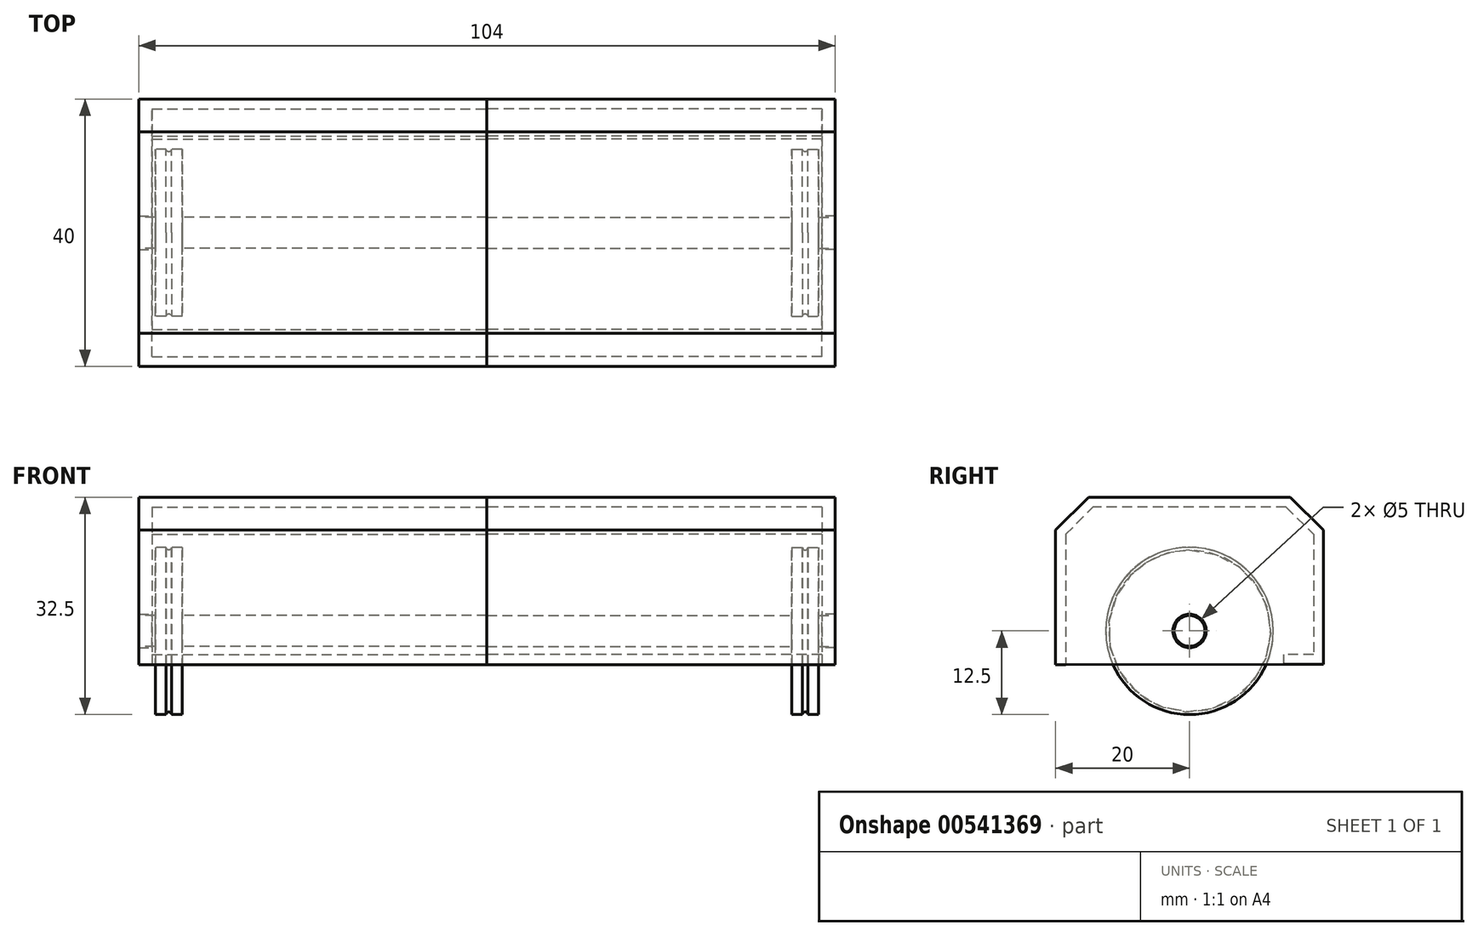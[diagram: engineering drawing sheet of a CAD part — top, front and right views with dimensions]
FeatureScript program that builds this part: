
annotation { "Feature Type Name" : "Feature", "Feature Type Description" : "" }
export const myFeature = defineFeature(function(context is Context, id is Id, definition is map)
    precondition{}
    {
        {
            var Q0;
            Q0=qCreatedBy(makeId("Right.planeOp"),FACE);
            var sketch = newSketch(context, id + "F0", { "sketchPlane" : qUnion([Q0])});
            skLineSegment(sketch, "E0", {"start": v(0, 0) * mm, "end": v(0, 20) * mm, "construction": true});
            skLineSegment(sketch, "E1", {"start": v(0, 20) * mm, "end": v(-15.05, 20) * mm});
            skCircle(sketch, "E2", {"center": v(0, 0) * mm, "radius": 12.5 * mm, "construction": true});
            skLineSegment(sketch, "E3", {"start": v(-20, 15.05) * mm, "end": v(-20, -5.07) * mm});
            skLineSegment(sketch, "E4", {"start": v(0, 20) * mm, "end": v(15.05, 20) * mm});
            skLineSegment(sketch, "E5", {"start": v(20, 15.05) * mm, "end": v(20, -5) * mm});
            skLineSegment(sketch, "E6", {"start": v(20, -5) * mm, "end": v(20, -5) * mm});
            skLineSegment(sketch, "E7", {"start": v(20, -5) * mm, "end": v(14, -5) * mm});
            skLineSegment(sketch, "E8.0", {"start": v(18.5, -3.5) * mm, "end": v(14, -3.5) * mm});
            skLineSegment(sketch, "E8.1", {"start": v(-18.5, 14.43) * mm, "end": v(-18.5, -5.07) * mm});
            skLineSegment(sketch, "E8.2", {"start": v(0.07, 18.5) * mm, "end": v(-14.43, 18.5) * mm});
            skLineSegment(sketch, "E8.3", {"start": v(0.07, 18.5) * mm, "end": v(14.43, 18.5) * mm});
            skLineSegment(sketch, "E8.4", {"start": v(18.5, 14.43) * mm, "end": v(18.5, -3.5) * mm});
            skLineSegment(sketch, "E9", {"start": v(-20, -5.07) * mm, "end": v(-18.5, -5.07) * mm});
            skLineSegment(sketch, "E10", {"start": v(14, -3.5) * mm, "end": v(14, -5) * mm});
            skPoint(sketch, "E11", {"position": v(-14.43, 18.5) * mm});
            skPoint(sketch, "E12", {"position": v(-18.5, 14.43) * mm});
            skLineSegment(sketch, "E13", {"start": v(-18.5, 14.43) * mm, "end": v(-14.43, 18.5) * mm});
            skPoint(sketch, "E14", {"position": v(-15.05, 20) * mm});
            skPoint(sketch, "E15", {"position": v(-20, 15.05) * mm});
            skLineSegment(sketch, "E16", {"start": v(-20, 15.05) * mm, "end": v(-15.05, 20) * mm});
            skLineSegment(sketch, "E17", {"start": v(-17.53, 17.53) * mm, "end": v(-16.46, 16.46) * mm, "construction": true});
            skPoint(sketch, "E18", {"position": v(14.43, 18.5) * mm});
            skPoint(sketch, "E19", {"position": v(18.5, 14.43) * mm});
            skPoint(sketch, "E20", {"position": v(15.05, 20) * mm});
            skPoint(sketch, "E21", {"position": v(20, 15.05) * mm});
            skLineSegment(sketch, "E22", {"start": v(14.43, 18.5) * mm, "end": v(18.5, 14.43) * mm});
            skLineSegment(sketch, "E23", {"start": v(15.05, 20) * mm, "end": v(20, 15.05) * mm});
            skPoint(sketch, "E24", {"position": v(16.46, 16.46) * mm});
            skPoint(sketch, "E25", {"position": v(17.53, 17.53) * mm});
            skLineSegment(sketch, "E26", {"start": v(16.46, 16.46) * mm, "end": v(17.53, 17.53) * mm, "construction": true});
            skSolve(sketch);
        }
        {
            var Q0;
            Q0=makeQuery(id+"F0.imprint","IMPRINT",FACE,{"disambiguationData":[TD([[makeQuery(id+"F0.imprint","IMPRINT",EDGE,{"derivedFrom":sQuery(id+"F0.wireOp",EDGE,"E1")}),1.0]])]});
            extrude(context, id + "F1", {"entities" : qUnion([Q0]), "depth" : 50 * mm, "offsetDistance" : 25 * mm});
        }
        {
            var Q0;
            Q0=makeQuery(id+"F1.opExtrude","CAP_FACE",FACE,{"disambiguationData":[OSD([sQuery(id+"F0.wireOp",EDGE,"E1"),sQuery(id+"F0.wireOp",EDGE,"E3"),sQuery(id+"F0.wireOp",EDGE,"E4"),sQuery(id+"F0.wireOp",EDGE,"E5"),sQuery(id+"F0.wireOp",EDGE,"E7"),sQuery(id+"F0.wireOp",EDGE,"E8.0"),sQuery(id+"F0.wireOp",EDGE,"E8.1"),sQuery(id+"F0.wireOp",EDGE,"E8.2"),sQuery(id+"F0.wireOp",EDGE,"E8.3"),sQuery(id+"F0.wireOp",EDGE,"E8.4"),sQuery(id+"F0.wireOp",EDGE,"E9"),sQuery(id+"F0.wireOp",EDGE,"E10")])],"isStart":false});
            var sketch = newSketch(context, id + "F2", { "sketchPlane" : qUnion([Q0])});
            skLineSegment(sketch, "E27.0.8", {"start": v(-20, -5.07) * mm, "end": v(-18.5, -5.07) * mm});
            skPoint(sketch, "E27.0.0.start.orphan", {"position": v(-14.43, 18.5) * mm});
            skPoint(sketch, "E27.0.1.start.orphan", {"position": v(14.43, 18.5) * mm});
            skPoint(sketch, "E27.0.2.start.orphan", {"position": v(18.5, -3.5) * mm});
            skPoint(sketch, "E27.0.3.start.orphan", {"position": v(14, -3.5) * mm});
            skCircle(sketch, "E28", {"center": v(0, 0) * mm, "radius": 2.5 * mm});
            skLineSegment(sketch, "E29.0", {"start": v(-20, 15.05) * mm, "end": v(-20, -5.07) * mm});
            skPoint(sketch, "E30.0", {"position": v(-17.53, 17.53) * mm});
            skLineSegment(sketch, "E31.0", {"start": v(-20, 15.05) * mm, "end": v(-15.05, 20) * mm});
            skLineSegment(sketch, "E32.0", {"start": v(0, 20) * mm, "end": v(-15.05, 20) * mm});
            skLineSegment(sketch, "E33.0", {"start": v(0, 20) * mm, "end": v(15.05, 20) * mm});
            skLineSegment(sketch, "E34.0", {"start": v(15.05, 20) * mm, "end": v(20, 15.05) * mm});
            skPoint(sketch, "E35.0", {"position": v(17.53, 17.53) * mm});
            skLineSegment(sketch, "E36.0", {"start": v(20, 15.05) * mm, "end": v(20, -5) * mm});
            skLineSegment(sketch, "E37.0", {"start": v(20, -5) * mm, "end": v(14, -5) * mm});
            skLineSegment(sketch, "E38", {"start": v(-18.5, -5.07) * mm, "end": v(14, -5) * mm});
            skSolve(sketch);
        }
        {
            var Q0;
            Q0 = qSketchRegion(id + "F2", true);
            extrude(context, id + "F3", {"entities" : qUnion([Q0]), "operationType" : NewBodyOperationType.ADD, "depth" : 2 * mm, "offsetDistance" : 25 * mm});
        }
        {
            var Q0;
            Q0=makeQuery(id+"F3.opExtrude","CAP_FACE",FACE,{"disambiguationData":[OSD([sQuery(id+"F2.wireOp",EDGE,"E27.0.5"),sQuery(id+"F2.wireOp",EDGE,"E27.0.6"),sQuery(id+"F2.wireOp",EDGE,"E27.0.7"),sQuery(id+"F2.wireOp",EDGE,"7a487413-c71e-4137-a8b7-0069e7eb67ab"),sQuery(id+"F2.wireOp",EDGE,"E28")])],"isStart":false});
            var sketch = newSketch(context, id + "F4", { "sketchPlane" : qUnion([Q0])});
            skCircle(sketch, "E39.0", {"center": v(0, 0) * mm, "radius": 2.3 * mm});
            skSolve(sketch);
        }
        {
            var Q0;
            Q0 = qSketchRegion(id + "F4", true);
            extrude(context, id + "F5", {"entities" : qUnion([Q0]), "oppositeDirection" : true, "depth" : 52 * mm, "offsetDistance" : 25 * mm});
        }
        {
            var Q0;
            Q0=makeQuery(id+"F3.opExtrude","CAP_FACE",FACE,{"disambiguationData":[OSD([sQuery(id+"F2.wireOp",EDGE,"E27.0.5"),sQuery(id+"F2.wireOp",EDGE,"E27.0.6"),sQuery(id+"F2.wireOp",EDGE,"E27.0.7"),sQuery(id+"F2.wireOp",EDGE,"7a487413-c71e-4137-a8b7-0069e7eb67ab"),sQuery(id+"F2.wireOp",EDGE,"E28")])],"isStart":false});
            cPlane(context, id + "F6", {"entities" : qUnion([Q0]), "cplaneType" : CPlaneType.OFFSET, "offset" : 2.5 * mm, "oppositeDirection" : true, "width" : 150 * mm, "height" : 150 * mm});
        }
        {
            var Q0;
            Q0=qCreatedBy(id+"F6.planeOp",FACE);
            var sketch = newSketch(context, id + "F7", { "sketchPlane" : qUnion([Q0])});
            skCircle(sketch, "E40.0", {"center": v(0, 0) * mm, "radius": 12.5 * mm});
            skSolve(sketch);
        }
        {
            var Q0;
            Q0 = qSketchRegion(id + "F7", true);
            extrude(context, id + "F8", {"entities" : qUnion([Q0]), "operationType" : NewBodyOperationType.ADD, "oppositeDirection" : true, "depth" : 4 * mm, "offsetDistance" : 25 * mm});
        }
        {
            var Q0;
            Q0=qCreatedBy(makeId("Top.planeOp"),FACE);
            cPlane(context, id + "F9", {"entities" : qUnion([Q0]), "cplaneType" : CPlaneType.OFFSET, "offset" : 0 * mm, "width" : 150 * mm, "height" : 150 * mm});
        }
        {
            var Q0;
            Q0=qCreatedBy(id+"F9.planeOp",FACE);
            var sketch = newSketch(context, id + "F10", { "sketchPlane" : qUnion([Q0])});
            skLineSegment(sketch, "E41", {"start": v(47.1, 12.5) * mm, "end": v(47.9, 12.5) * mm});
            skPoint(sketch, "E42.0.end.orphan", {"position": v(45.5, -12.5) * mm});
            skPoint(sketch, "E43.0.end.orphan", {"position": v(49.5, -12.5) * mm});
            skArc(sketch, "E44", {"start": v(47.1, 12.5) * mm, "mid": v(47.5, 12.1) * mm, "end": v(47.9, 12.5) * mm});
            skPoint(sketch, "E45.orphan", {"position": v(45.5, 12.5) * mm});
            skPoint(sketch, "E46.orphan", {"position": v(49.5, 12.5) * mm});
            skSolve(sketch);
        }
        {
            var Q0;
            Q0=makeQuery(id+"F8.opExtrude","CAP_FACE",FACE,{"disambiguationData":[OSD([sQuery(id+"F7.wireOp",EDGE,"E40.0")])],"isStart":true});
            cPlane(context, id + "F11", {"entities" : qUnion([Q0]), "cplaneType" : CPlaneType.OFFSET, "offset" : 2 * mm, "oppositeDirection" : true, "width" : 150 * mm, "height" : 150 * mm});
        }
        {
            var Q0;
            Q0=qCreatedBy(makeId("Top.planeOp"),FACE);
            var sketch = newSketch(context, id + "F12", { "sketchPlane" : qUnion([Q0])});
            skLineSegment(sketch, "E47", {"start": v(0, 0) * mm, "end": v(42.92, 0) * mm});
            skSolve(sketch);
        }
        {
            var Q0;
            Q0=makeQuery(id+"F10.imprint","IMPRINT",FACE,{"disambiguationData":[TD([[makeQuery(id+"F10.imprint","IMPRINT",EDGE,{"derivedFrom":sQuery(id+"F10.wireOp",EDGE,"E41")}),-1.0]])]});
            var Q1;
            Q1=sQuery(id+"F10.wireOp",EDGE,"E44");
            var Q2;
            Q2=sQuery(id+"F10.wireOp",EDGE,"E41");
            var Q3;
            Q3=sQuery(id+"F12.wireOp",EDGE,"E47");
            revolve(context, id + "F13", {"operationType" : NewBodyOperationType.REMOVE, "entities" : qUnion([Q0]), "surfaceEntities" : qUnion([Q1, Q2]), "axis" : qUnion([Q3]), "revolveType" : RevolveType.FULL});
        }
        {
            var Q0;
            Q0=makeQuery(id+"F1.opExtrude","SWEPT_BODY",BODY,{"disambiguationData":[OSD([sQuery(id+"F0.wireOp",EDGE,"E1"),sQuery(id+"F0.wireOp",EDGE,"E3"),sQuery(id+"F0.wireOp",EDGE,"E4"),sQuery(id+"F0.wireOp",EDGE,"E5"),sQuery(id+"F0.wireOp",EDGE,"E7"),sQuery(id+"F0.wireOp",EDGE,"E8.0"),sQuery(id+"F0.wireOp",EDGE,"E8.1"),sQuery(id+"F0.wireOp",EDGE,"E8.2"),sQuery(id+"F0.wireOp",EDGE,"E8.3"),sQuery(id+"F0.wireOp",EDGE,"E8.4"),sQuery(id+"F0.wireOp",EDGE,"E9"),sQuery(id+"F0.wireOp",EDGE,"E10")])]});
            var Q1;
            Q1=qCreatedBy(makeId("Right.planeOp"),FACE);
            mirror(context, id + "F14", {"operationType" : NewBodyOperationType.ADD, "entities" : qUnion([Q0]), "mirrorPlane" : qUnion([Q1])});
        }
        {
            var Q0;
            Q0=makeQuery(id+"F5.opExtrude","SWEPT_BODY",BODY,{"disambiguationData":[OSD([sQuery(id+"F4.wireOp",EDGE,"E39.0")])]});
            var Q1;
            Q1=qCreatedBy(makeId("Right.planeOp"),FACE);
            mirror(context, id + "F15", {"operationType" : NewBodyOperationType.ADD, "entities" : qUnion([Q0]), "mirrorPlane" : qUnion([Q1])});
        }
    });
